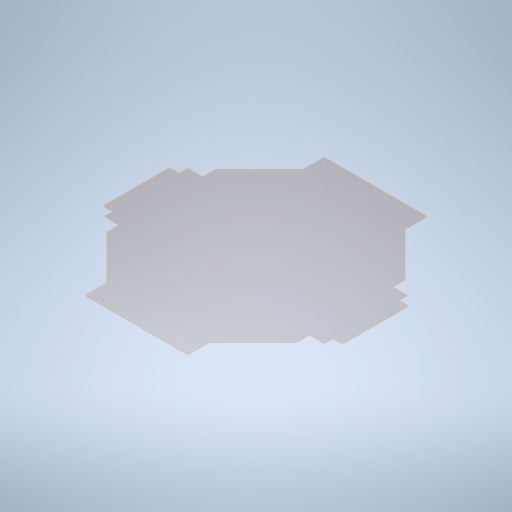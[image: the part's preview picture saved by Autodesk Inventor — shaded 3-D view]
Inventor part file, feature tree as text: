
AUTODESK INVENTOR PART (.ipt)
format: ipt  version: 2023.4 (Build 274418000, 418)  size: 448,000 bytes
history: native  units: in
note: dims shown in document units (in); Inventor stores cm internally (conversion verified against a paired STEP export)
features: sketch x3, extrude x2, hole x1, fillet x1, projected_geometry x1
ambient origin geometry x8: Origin, YZ Plane, XZ Plane, XY Plane, X Axis, Y Axis, Z Axis, Center Point
bodies: Solid1 (feature_tree)
feature tree (8):
  extrude  "Extrusion1"  Depth=28.0in
  hole  "Hole1"  [1 undecoded]
  extrude  "Extrusion2"  Depth=0.125in TaperAngle=0.0deg
  fillet  "Fillet1"  Radius=0.5in
  sketch  "Sketch1"  dims[d0=28.0in d1=28.0in]
  sketch  "Sketch2"  dims[d2=2.5in d3=8.0in]
  sketch  "Sketch3"  dims[d4=1.5748in d6=360.0deg d8=0.125in d9=0.0in d10=0.5in d11=0.5in d12=0.5in d13=0.5in d14=0.5in d15=0.5in d16=4.7244in d18=1.0in d19=0.3937in d21=1.0in d23=4.7244in d25=1.0in d26=0.3937in d28=1.0in d30=0.201in d31=0.75in d32=0.385in d33=0.25in d34=0.5635in d35=1.0in d36=0.8108in d37=0.0in d38=0.0in d39=2.125in d40=1.125in d42=1.125in d43=2.875in d44=0.13in]
  projected_geometry  "Projected Loop1"
note: 1 required parameter value undecoded (feature->parameter linkage not recoverable at this tier; creation-order binding heuristic only, values carry confidence <= 0.55)
